# Revit family: Site-Waste_Management-EarthBin-EB500T-bk1
name_source: partatom
category: Site
units: mm (PartAtom-declared; Revit-internal decimal feet)

## family parameters
Always vertical = Yes
Cut with Voids When Loaded = No
OmniClass Number = 23.70.30.21.14
OmniClass Title = Solid Waste Bins
Part Type = Normal
Round Connector Dimension = Use Diameter
Shared = No
Work Plane-Based = No

## types (4) — shared parameters
Assembly Code = E1090200
CD_Depth In Ground = 5' - 0"
CD_Diameter = 5' - 10 13/16"
CD_Feed Height = 3' - 3 13/32"
CD_Finish Feed Door = Plastic-Polyethylene-EarthBin-Feed_Door-Blue
CD_Finish Frame = Metal-Steel-EarthBin
CD_Finish Lid = Plastic-Polyethylene-EarthBin-Lid-Grey
CD_Height = 4' - 0 1/2"
CD_Microsite = https://www.caddetails.com
CD_Product Documentation Link = https://static1.squarespace.com
CD_Product Name = Crane Lifted Semi In-Ground Silo 500T
CD_Product Page URL = https://www.earthbin.com
CD_Specification = https://static1.squarespace.com
Default Elevation = 0' - 0"
Description = Round waste & recycling
Manufacturer = EarthBin
Model = EB500T
Type Comments = 5000 litre (6.5 cubic yard)
URL = https://www.earthbin.com

## per-type parameters (varying)
| type | CD_Finish Bin |
| Dark Brown | Plastic-Polyethylene-EarthBin-Panel_Narrow-Dark_Brown |
| Black | Plastic-Polyethylene-EarthBin-Panel_Narrow-Black |
| Cedar | Plastic-Polyethylene-EarthBin-Panel_Narrow-Cedar |
| Dark Grey | Plastic-Polyethylene-EarthBin-Panel_Narrow-Dark_Grey |

## geometry (parser evidence)
native form markers: Sweep x6
no freeform markers — native parametric forms only
